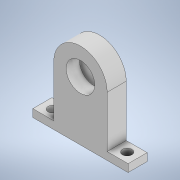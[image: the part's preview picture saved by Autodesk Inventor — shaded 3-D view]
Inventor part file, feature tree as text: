
AUTODESK INVENTOR PART (.ipt)
format: ipt  version: 2021 (Build 250183000, 183)  size: 131,584 bytes
history: native  units: mm
features: extrude x3, sketch x3, other x1
ambient origin geometry x8: Origin, YZ Plane, XZ Plane, XY Plane, X Axis, Y Axis, Z Axis, Center Point
bodies: Body1 (feature_tree)
feature tree (7):
  other  "Sólido1"
  extrude  "Extrusión1"  Depth=7.5mm
  extrude  "Extrusión2"  Depth=5.0mm TaperAngle=0.0deg
  extrude  "Extrusión3"  Depth=28.0mm
  sketch  "Boceto1"  dims[d0=10.0mm d1=0.0mm d2=7.5mm]
  sketch  "Boceto2"  dims[d3=5.0mm d4=5.0mm d5=0.0mm]
  sketch  "Boceto3"  dims[d6=50.0mm d7=28.0mm d8=15.0mm d9=7.0mm d10=0.0mm d11=20.594885mm d12=0.0625mm d13=0.75mm d14=0.375mm]
